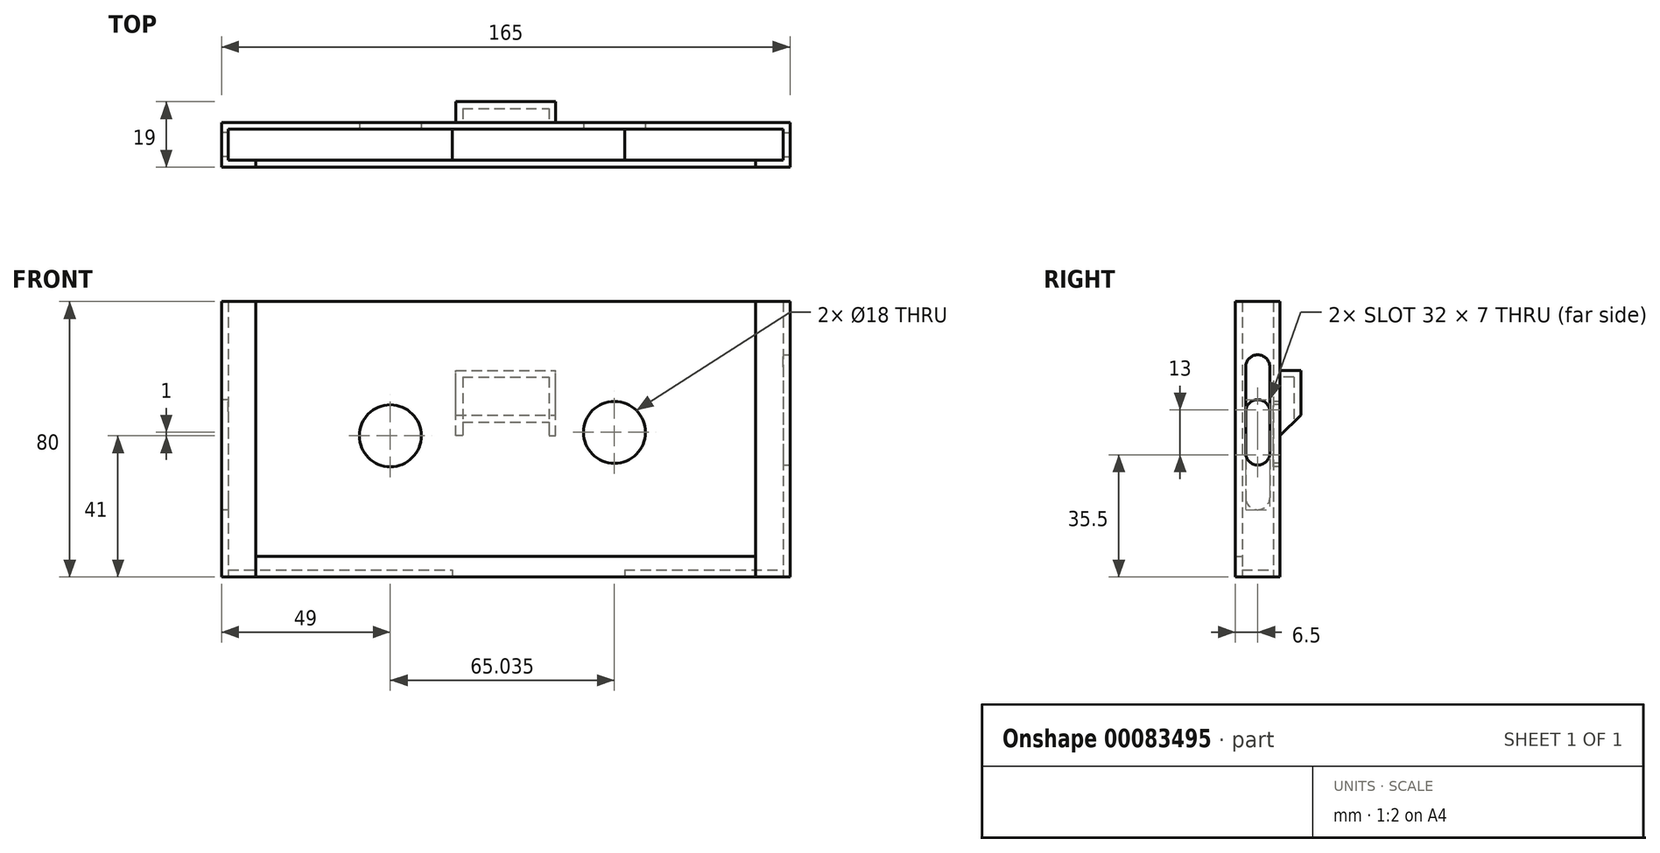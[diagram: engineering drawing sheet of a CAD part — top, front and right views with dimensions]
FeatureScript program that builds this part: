
annotation { "Feature Type Name" : "Feature", "Feature Type Description" : "" }
export const myFeature = defineFeature(function(context is Context, id is Id, definition is map)
    precondition{}
    {
        {
            var Q0;
            Q0=qCreatedBy(makeId("Top.planeOp"),FACE);
            var sketch = newSketch(context, id + "F0", { "sketchPlane" : qUnion([Q0])});
            skLineSegment(sketch, "E0", {"start": v(0, 0) * mm, "end": v(161, 0) * mm});
            skLineSegment(sketch, "E1", {"start": v(161, 0) * mm, "end": v(161, 9) * mm});
            skLineSegment(sketch, "E2", {"start": v(161, 9) * mm, "end": v(0, 9) * mm});
            skLineSegment(sketch, "E3", {"start": v(0, 9) * mm, "end": v(0, 0) * mm});
            skLineSegment(sketch, "E4", {"start": v(0, 9) * mm, "end": v(0, 11) * mm});
            skLineSegment(sketch, "E5", {"start": v(161, 9) * mm, "end": v(161, 11) * mm});
            skLineSegment(sketch, "E6", {"start": v(0, 9) * mm, "end": v(-2, 9) * mm});
            skLineSegment(sketch, "E7", {"start": v(0, 0) * mm, "end": v(-2, 0) * mm});
            skLineSegment(sketch, "E8", {"start": v(0, 0) * mm, "end": v(0, -2) * mm});
            skLineSegment(sketch, "E9", {"start": v(161, 0) * mm, "end": v(161, -2) * mm});
            skLineSegment(sketch, "E10", {"start": v(161, 0) * mm, "end": v(163, 0) * mm});
            skLineSegment(sketch, "E11", {"start": v(161, 9) * mm, "end": v(163, 9) * mm});
            skLineSegment(sketch, "E12", {"start": v(-2, 11) * mm, "end": v(0, 11) * mm});
            skLineSegment(sketch, "E13", {"start": v(-2, 9) * mm, "end": v(-2, 11) * mm});
            skLineSegment(sketch, "E14", {"start": v(-2, 0) * mm, "end": v(-2, -2) * mm});
            skLineSegment(sketch, "E15", {"start": v(-2, -2) * mm, "end": v(0, -2) * mm});
            skLineSegment(sketch, "E16", {"start": v(-2, 0) * mm, "end": v(-2, 9) * mm});
            skLineSegment(sketch, "E17", {"start": v(0, 11) * mm, "end": v(161, 11) * mm});
            skLineSegment(sketch, "E18", {"start": v(163, 11) * mm, "end": v(163, 9) * mm});
            skLineSegment(sketch, "E19", {"start": v(161, 11) * mm, "end": v(163, 11) * mm});
            skLineSegment(sketch, "E20", {"start": v(163, 9) * mm, "end": v(163, 0) * mm});
            skLineSegment(sketch, "E21", {"start": v(163, 0) * mm, "end": v(163, -2) * mm});
            skLineSegment(sketch, "E22", {"start": v(163, -2) * mm, "end": v(161, -2) * mm});
            skLineSegment(sketch, "E23", {"start": v(161, -2) * mm, "end": v(0, -2) * mm});
            skLineSegment(sketch, "E24", {"start": v(0, 0) * mm, "end": v(8, 0) * mm});
            skLineSegment(sketch, "E25", {"start": v(8, 0) * mm, "end": v(8, -2) * mm});
            skLineSegment(sketch, "E26", {"start": v(163, -2) * mm, "end": v(153, -2) * mm});
            skLineSegment(sketch, "E27", {"start": v(153, -2) * mm, "end": v(153, 0) * mm});
            skSolve(sketch);
        }
        {
            var Q0;
            Q0=makeQuery(id+"F0.imprint","IMPRINT",FACE,{"disambiguationData":[TD([[makeQuery(id+"F0.imprint","IMPRINT",EDGE,{"derivedFrom":sQuery(id+"F0.wireOp",EDGE,"E2")}),-1.0]])]});
            var Q1;
            Q1=makeQuery(id+"F0.imprint","IMPRINT",FACE,{"disambiguationData":[TD([[makeQuery(id+"F0.imprint","IMPRINT",EDGE,{"derivedFrom":sQuery(id+"F0.wireOp",EDGE,"E5")}),-1.0]])]});
            var Q2;
            Q2=makeQuery(id+"F0.imprint","IMPRINT",FACE,{"disambiguationData":[TD([[makeQuery(id+"F0.imprint","IMPRINT",EDGE,{"derivedFrom":sQuery(id+"F0.wireOp",EDGE,"E1")}),-1.0]])]});
            var Q3;
            Q3=makeQuery(id+"F0.imprint","IMPRINT",FACE,{"disambiguationData":[TD([[makeQuery(id+"F0.imprint","IMPRINT",EDGE,{"derivedFrom":sQuery(id+"F0.wireOp",EDGE,"E9")}),1.0]])]});
            var Q4;
            {var subQ0=sQuery(id+"F0.wireOp",EDGE,"E9");Q4=makeQuery(id+"F0.imprint","IMPRINT",FACE,{"disambiguationData":[TD([[makeQuery(id+"F0.imprint","IMPRINT",EDGE,{"derivedFrom":subQ0}),-1.0]])]});}
            var Q5;
            Q5=makeQuery(id+"F0.imprint","IMPRINT",FACE,{"disambiguationData":[TD([[makeQuery(id+"F0.imprint","IMPRINT",EDGE,{"derivedFrom":sQuery(id+"F0.wireOp",EDGE,"E4")}),1.0]])]});
            var Q6;
            Q6=makeQuery(id+"F0.imprint","IMPRINT",FACE,{"disambiguationData":[TD([[makeQuery(id+"F0.imprint","IMPRINT",EDGE,{"derivedFrom":sQuery(id+"F0.wireOp",EDGE,"E3")}),-1.0]])]});
            var Q7;
            Q7=makeQuery(id+"F0.imprint","IMPRINT",FACE,{"disambiguationData":[TD([[makeQuery(id+"F0.imprint","IMPRINT",EDGE,{"derivedFrom":sQuery(id+"F0.wireOp",EDGE,"E7")}),1.0]])]});
            var Q8;
            {var subQ2=sQuery(id+"F0.wireOp",EDGE,"E8");Q8=makeQuery(id+"F0.imprint","IMPRINT",FACE,{"disambiguationData":[TD([[makeQuery(id+"F0.imprint","IMPRINT",EDGE,{"derivedFrom":subQ2}),1.0]])]});}
            extrude(context, id + "F1", {"entities" : qUnion([Q0, Q1, Q2, Q3, Q4, Q5, Q6, Q7, Q8]), "depth" : 80 * mm});
        }
        {
            var Q0;
            {var subQ0=sQuery(id+"F0.wireOp",EDGE,"E1");Q0=makeQuery(id+"F0.imprint","IMPRINT",FACE,{"disambiguationData":[TD([[makeQuery(id+"F0.imprint","IMPRINT",EDGE,{"derivedFrom":subQ0}),1.0]])]});}
            extrude(context, id + "F2", {"entities" : qUnion([Q0]), "depth" : 2 * mm});
        }
        {
            var Q0;
            {var subQ0=sQuery(id+"F0.wireOp",EDGE,"E25");Q0=makeQuery(id+"F0.imprint","IMPRINT",FACE,{"disambiguationData":[TD([[makeQuery(id+"F0.imprint","IMPRINT",EDGE,{"derivedFrom":subQ0}),1.0]])]});}
            extrude(context, id + "F3", {"entities" : qUnion([Q0]), "depth" : 6 * mm});
        }
        {
            var Q0;
            Q0=makeQuery(id+"F1.opExtrude","SWEPT_FACE",FACE,{"disambiguationData":[OSD([sQuery(id+"F0.wireOp",EDGE,"E13"),sQuery(id+"F0.wireOp",EDGE,"E14"),sQuery(id+"F0.wireOp",EDGE,"E16")])]});
            var sketch = newSketch(context, id + "F4", { "sketchPlane" : qUnion([Q0])});
            skPoint(sketch, "E28", {"position": v(-4.5, 23) * mm});
            skPoint(sketch, "E29", {"position": v(2, 23) * mm});
            skPoint(sketch, "E30", {"position": v(-4.5, 0) * mm});
            skPoint(sketch, "E31", {"position": v(-4.5, 48) * mm});
            skLineSegment(sketch, "E32.bottom", {"start": v(-8, 48) * mm, "end": v(-1, 48) * mm});
            skLineSegment(sketch, "E32.top", {"start": v(-8, 23) * mm, "end": v(-1, 23) * mm});
            skLineSegment(sketch, "E32.left", {"start": v(-8, 48) * mm, "end": v(-8, 23) * mm});
            skLineSegment(sketch, "E32.right", {"start": v(-1, 48) * mm, "end": v(-1, 23) * mm});
            skArc(sketch, "E33", {"start": v(-1, 48) * mm, "mid": v(-4.5, 51.5) * mm, "end": v(-8, 48) * mm});
            skArc(sketch, "E34", {"start": v(-8, 23) * mm, "mid": v(-4.5, 19.5) * mm, "end": v(-1, 23) * mm});
            skSolve(sketch);
        }
        {
            var Q0;
            Q0=makeQuery(id+"F4.imprint","IMPRINT",FACE,{"disambiguationData":[TD([[makeQuery(id+"F4.imprint","IMPRINT",EDGE,{"derivedFrom":sQuery(id+"F4.wireOp",EDGE,"E32.bottom")}),1.0]])]});
            var Q1;
            Q1=makeQuery(id+"F4.imprint","IMPRINT",FACE,{"disambiguationData":[TD([[makeQuery(id+"F4.imprint","IMPRINT",EDGE,{"derivedFrom":sQuery(id+"F4.wireOp",EDGE,"E32.bottom")}),-1.0]])]});
            var Q2;
            Q2=makeQuery(id+"F4.imprint","IMPRINT",FACE,{"disambiguationData":[TD([[makeQuery(id+"F4.imprint","IMPRINT",EDGE,{"derivedFrom":sQuery(id+"F4.wireOp",EDGE,"E32.top")}),-1.0]])]});
            extrude(context, id + "F5", {"entities" : qUnion([Q0, Q1, Q2]), "operationType" : NewBodyOperationType.REMOVE, "endBound" : BoundingType.UP_TO_NEXT, "oppositeDirection" : true, "depth" : 25 * mm});
        }
        {
            var Q0;
            Q0=makeQuery(id+"F1.opExtrude","SWEPT_FACE",FACE,{"disambiguationData":[OSD([sQuery(id+"F0.wireOp",EDGE,"E18"),sQuery(id+"F0.wireOp",EDGE,"E20"),sQuery(id+"F0.wireOp",EDGE,"E21")])]});
            var sketch = newSketch(context, id + "F6", { "sketchPlane" : qUnion([Q0])});
            skPoint(sketch, "E35", {"position": v(4.5, 36) * mm});
            skPoint(sketch, "E36", {"position": v(11, 36) * mm});
            skPoint(sketch, "E37", {"position": v(4.5, 0) * mm});
            skPoint(sketch, "E38", {"position": v(4.5, 61) * mm});
            skLineSegment(sketch, "E39.bottom", {"start": v(1, 61) * mm, "end": v(8, 61) * mm});
            skLineSegment(sketch, "E39.top", {"start": v(1, 36) * mm, "end": v(8, 36) * mm});
            skLineSegment(sketch, "E39.left", {"start": v(1, 61) * mm, "end": v(1, 36) * mm});
            skLineSegment(sketch, "E39.right", {"start": v(8, 61) * mm, "end": v(8, 36) * mm});
            skArc(sketch, "E40", {"start": v(8, 61) * mm, "mid": v(4.5, 64.5) * mm, "end": v(1, 61) * mm});
            skArc(sketch, "E41", {"start": v(1, 36) * mm, "mid": v(4.5, 32.5) * mm, "end": v(8, 36) * mm});
            skSolve(sketch);
        }
        {
            var Q0;
            Q0=makeQuery(id+"F6.imprint","IMPRINT",FACE,{"disambiguationData":[TD([[makeQuery(id+"F6.imprint","IMPRINT",EDGE,{"derivedFrom":sQuery(id+"F6.wireOp",EDGE,"E39.bottom")}),1.0]])]});
            var Q1;
            Q1=makeQuery(id+"F6.imprint","IMPRINT",FACE,{"disambiguationData":[TD([[makeQuery(id+"F6.imprint","IMPRINT",EDGE,{"derivedFrom":sQuery(id+"F6.wireOp",EDGE,"E39.bottom")}),-1.0]])]});
            var Q2;
            Q2=makeQuery(id+"F6.imprint","IMPRINT",FACE,{"disambiguationData":[TD([[makeQuery(id+"F6.imprint","IMPRINT",EDGE,{"derivedFrom":sQuery(id+"F6.wireOp",EDGE,"E39.top")}),-1.0]])]});
            extrude(context, id + "F7", {"entities" : qUnion([Q0, Q1, Q2]), "operationType" : NewBodyOperationType.REMOVE, "endBound" : BoundingType.UP_TO_NEXT, "oppositeDirection" : true, "depth" : 25 * mm});
        }
        {
            var Q0;
            Q0=qCreatedBy(makeId("Front.planeOp"),FACE);
            var sketch = newSketch(context, id + "F8", { "sketchPlane" : qUnion([Q0])});
            skPoint(sketch, "E42", {"position": v(47, 0) * mm});
            skPoint(sketch, "E43", {"position": v(47, 41) * mm});
            skCircle(sketch, "E44", {"center": v(47, 41) * mm, "radius": 9 * mm});
            skPoint(sketch, "E45", {"position": v(113, 0) * mm});
            skPoint(sketch, "E46", {"position": v(112.04, 42) * mm});
            skCircle(sketch, "E47", {"center": v(112.04, 42) * mm, "radius": 9 * mm});
            skSolve(sketch);
        }
        {
            var Q0;
            Q0=makeQuery(id+"F8.imprint","IMPRINT",FACE,{"disambiguationData":[TD([[makeQuery(id+"F8.imprint","IMPRINT",EDGE,{"derivedFrom":sQuery(id+"F8.wireOp",EDGE,"E44")}),1.0]])]});
            var Q1;
            Q1=makeQuery(id+"F8.imprint","IMPRINT",FACE,{"disambiguationData":[TD([[makeQuery(id+"F8.imprint","IMPRINT",EDGE,{"derivedFrom":sQuery(id+"F8.wireOp",EDGE,"E47")}),1.0]])]});
            extrude(context, id + "F9", {"entities" : qUnion([Q0, Q1]), "operationType" : NewBodyOperationType.REMOVE, "endBound" : BoundingType.THROUGH_ALL, "oppositeDirection" : true, "depth" : 25 * mm});
        }
        {
            var Q0;
            Q0=makeQuery(id+"F1.opExtrude","SWEPT_FACE",FACE,{"disambiguationData":[OSD([sQuery(id+"F0.wireOp",EDGE,"E12"),sQuery(id+"F0.wireOp",EDGE,"E17"),sQuery(id+"F0.wireOp",EDGE,"E19")])]});
            var sketch = newSketch(context, id + "F10", { "sketchPlane" : qUnion([Q0])});
            skPoint(sketch, "E48", {"position": v(-80.5, 58) * mm});
            skLineSegment(sketch, "E49", {"start": v(-80.5, 58) * mm, "end": v(-68, 58) * mm});
            skLineSegment(sketch, "E50", {"start": v(-68, 58) * mm, "end": v(-68, 47) * mm});
            skLineSegment(sketch, "E51", {"start": v(-68, 47) * mm, "end": v(-68, 41) * mm});
            skLineSegment(sketch, "E52", {"start": v(-80.5, 58) * mm, "end": v(-93, 58) * mm});
            skLineSegment(sketch, "E53", {"start": v(-93, 58) * mm, "end": v(-93, 47) * mm});
            skLineSegment(sketch, "E54", {"start": v(-93, 47) * mm, "end": v(-93, 41) * mm});
            skLineSegment(sketch, "E55", {"start": v(-93, 41) * mm, "end": v(-95, 41) * mm});
            skLineSegment(sketch, "E56", {"start": v(-95, 41) * mm, "end": v(-95, 58) * mm});
            skLineSegment(sketch, "E57", {"start": v(-95, 58) * mm, "end": v(-93, 58) * mm});
            skLineSegment(sketch, "E58", {"start": v(-68, 41) * mm, "end": v(-66, 41) * mm});
            skLineSegment(sketch, "E59", {"start": v(-66, 41) * mm, "end": v(-66, 58) * mm});
            skLineSegment(sketch, "E60", {"start": v(-66, 58) * mm, "end": v(-68, 58) * mm});
            skLineSegment(sketch, "E61", {"start": v(-93, 47) * mm, "end": v(-95, 47) * mm});
            skLineSegment(sketch, "E62", {"start": v(-68, 47) * mm, "end": v(-66, 47) * mm});
            skLineSegment(sketch, "E63", {"start": v(-66, 58) * mm, "end": v(-66, 60) * mm});
            skLineSegment(sketch, "E64", {"start": v(-66, 60) * mm, "end": v(-68, 60) * mm});
            skLineSegment(sketch, "E65", {"start": v(-68, 60) * mm, "end": v(-93, 60) * mm});
            skLineSegment(sketch, "E66", {"start": v(-93, 60) * mm, "end": v(-95, 60) * mm});
            skLineSegment(sketch, "E67", {"start": v(-95, 60) * mm, "end": v(-95, 58) * mm});
            skLineSegment(sketch, "E68", {"start": v(-93, 58) * mm, "end": v(-93, 60) * mm});
            skLineSegment(sketch, "E69", {"start": v(-68, 58) * mm, "end": v(-68, 60) * mm});
            skSolve(sketch);
        }
        {
            var Q0;
            Q0=makeQuery(id+"F10.imprint","IMPRINT",FACE,{"disambiguationData":[TD([[makeQuery(id+"F10.imprint","IMPRINT",EDGE,{"derivedFrom":sQuery(id+"F10.wireOp",EDGE,"E54")}),-1.0]])]});
            var Q1;
            Q1=makeQuery(id+"F10.imprint","IMPRINT",FACE,{"disambiguationData":[TD([[makeQuery(id+"F10.imprint","IMPRINT",EDGE,{"derivedFrom":sQuery(id+"F10.wireOp",EDGE,"E53")}),-1.0]])]});
            var Q2;
            Q2=makeQuery(id+"F10.imprint","IMPRINT",FACE,{"disambiguationData":[TD([[makeQuery(id+"F10.imprint","IMPRINT",EDGE,{"derivedFrom":sQuery(id+"F10.wireOp",EDGE,"E57")}),1.0]])]});
            var Q3;
            Q3=makeQuery(id+"F10.imprint","IMPRINT",FACE,{"disambiguationData":[TD([[makeQuery(id+"F10.imprint","IMPRINT",EDGE,{"derivedFrom":sQuery(id+"F10.wireOp",EDGE,"E49")}),1.0]])]});
            var Q4;
            Q4=makeQuery(id+"F10.imprint","IMPRINT",FACE,{"disambiguationData":[TD([[makeQuery(id+"F10.imprint","IMPRINT",EDGE,{"derivedFrom":sQuery(id+"F10.wireOp",EDGE,"E60")}),-1.0]])]});
            var Q5;
            Q5=makeQuery(id+"F10.imprint","IMPRINT",FACE,{"disambiguationData":[TD([[makeQuery(id+"F10.imprint","IMPRINT",EDGE,{"derivedFrom":sQuery(id+"F10.wireOp",EDGE,"E50")}),1.0]])]});
            var Q6;
            Q6=makeQuery(id+"F10.imprint","IMPRINT",FACE,{"disambiguationData":[TD([[makeQuery(id+"F10.imprint","IMPRINT",EDGE,{"derivedFrom":sQuery(id+"F10.wireOp",EDGE,"E51")}),1.0]])]});
            extrude(context, id + "F11", {"entities" : qUnion([Q0, Q1, Q2, Q3, Q4, Q5, Q6]), "operationType" : NewBodyOperationType.ADD, "depth" : 6 * mm});
        }
        {
            var Q0;
            Q0=makeQuery(id+"F11.opExtrude","SWEPT_FACE",FACE,{"disambiguationData":[OSD([sQuery(id+"F10.wireOp",EDGE,"E53"),sQuery(id+"F10.wireOp",EDGE,"E54")])]});
            var sketch = newSketch(context, id + "F12", { "sketchPlane" : qUnion([Q0])});
            skLineSegment(sketch, "E70", {"start": v(-17, 58) * mm, "end": v(-15, 58) * mm});
            skLineSegment(sketch, "E71", {"start": v(-15, 58) * mm, "end": v(-15, 47) * mm});
            skLineSegment(sketch, "E72", {"start": v(-15, 47) * mm, "end": v(-15, 41) * mm});
            skLineSegment(sketch, "E73", {"start": v(-15, 41) * mm, "end": v(-17, 41) * mm});
            skLineSegment(sketch, "E74", {"start": v(-17, 41) * mm, "end": v(-17, 58) * mm});
            skSolve(sketch);
        }
        {
            var Q0;
            Q0=makeQuery(id+"F12.imprint","IMPRINT",FACE,{"disambiguationData":[TD([[makeQuery(id+"F12.imprint","IMPRINT",EDGE,{"derivedFrom":sQuery(id+"F12.wireOp",EDGE,"E71")}),-1.0]])]});
            extrude(context, id + "F13", {"entities" : qUnion([Q0]), "operationType" : NewBodyOperationType.ADD, "endBound" : BoundingType.UP_TO_NEXT, "depth" : 25 * mm});
        }
        {
            var Q0;
            Q0=makeQuery(id+"F11.opExtrude","SWEPT_FACE",FACE,{"disambiguationData":[OSD([sQuery(id+"F10.wireOp",EDGE,"E56"),sQuery(id+"F10.wireOp",EDGE,"E67")])]});
            var sketch = newSketch(context, id + "F14", { "sketchPlane" : qUnion([Q0])});
            skLineSegment(sketch, "E75", {"start": v(11, 41) * mm, "end": v(17, 47) * mm});
            skSolve(sketch);
        }
        {
            var Q0;
            {var subQ0=sQuery(id+"F14.wireOp",EDGE,"E75");Q0=makeQuery(id+"F14.imprint","IMPRINT",FACE,{"disambiguationData":[TD([[makeQuery(id+"F14.imprint","IMPRINT",EDGE,{"derivedFrom":subQ0}),-1.0]])]});}
            extrude(context, id + "F15", {"entities" : qUnion([Q0]), "operationType" : NewBodyOperationType.REMOVE, "endBound" : BoundingType.THROUGH_ALL, "oppositeDirection" : true, "depth" : 25 * mm});
        }
        {
            var Q0;
            {var subQ0=sQuery(id+"F0.wireOp",EDGE,"E1");Q0=makeQuery(id+"F0.imprint","IMPRINT",FACE,{"disambiguationData":[TD([[makeQuery(id+"F0.imprint","IMPRINT",EDGE,{"derivedFrom":subQ0}),1.0]])]});}
            var sketch = newSketch(context, id + "F16", { "sketchPlane" : qUnion([Q0])});
            skLineSegment(sketch, "E76", {"start": v(0, 0) * mm, "end": v(65, 0) * mm});
            skLineSegment(sketch, "E77", {"start": v(115, 0) * mm, "end": v(65, 0) * mm});
            skLineSegment(sketch, "E78", {"start": v(115, 0) * mm, "end": v(115, 9) * mm});
            skLineSegment(sketch, "E79", {"start": v(115, 9) * mm, "end": v(65, 9) * mm});
            skLineSegment(sketch, "E80", {"start": v(65, 9) * mm, "end": v(65, 0) * mm});
            skSolve(sketch);
        }
        {
            var Q0;
            Q0=makeQuery(id+"F16.imprint","IMPRINT",FACE,{"disambiguationData":[TD([[makeQuery(id+"F16.imprint","IMPRINT",EDGE,{"derivedFrom":sQuery(id+"F16.wireOp",EDGE,"E77")}),1.0]])]});
            extrude(context, id + "F17", {"entities" : qUnion([Q0]), "operationType" : NewBodyOperationType.REMOVE, "endBound" : BoundingType.UP_TO_NEXT, "depth" : 10 * mm, "offsetDistance" : 25 * mm});
        }
    });
